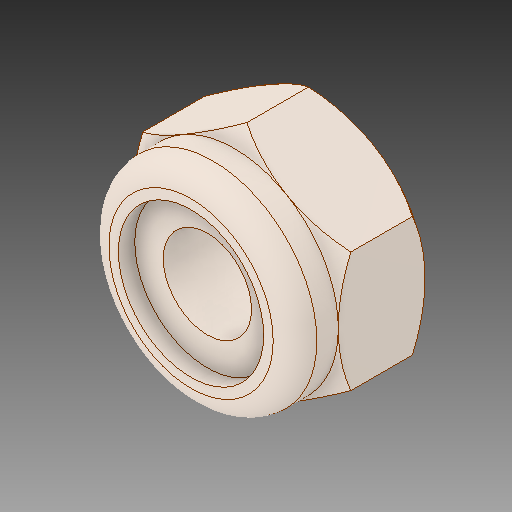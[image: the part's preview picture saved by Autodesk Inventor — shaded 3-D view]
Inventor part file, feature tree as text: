
AUTODESK INVENTOR PART (.ipt)
format: ipt  version: 2018.2 (Build 222227000, 227)  size: 167,424 bytes
history: native  units: in
note: dims shown in document units (in); Inventor stores cm internally (conversion verified against a paired STEP export)
features: fillet x1
ambient origin geometry x8: Origin, YZ Plane, XZ Plane, XY Plane, X Axis, Y Axis, Z Axis, Center Point
bodies: Solid1 (feature_tree)
feature tree (1):
  fillet  "Fillet1"  [1 undecoded]
note: 1 required parameter value undecoded (feature->parameter linkage not recoverable at this tier; creation-order binding heuristic only, values carry confidence <= 0.55)
